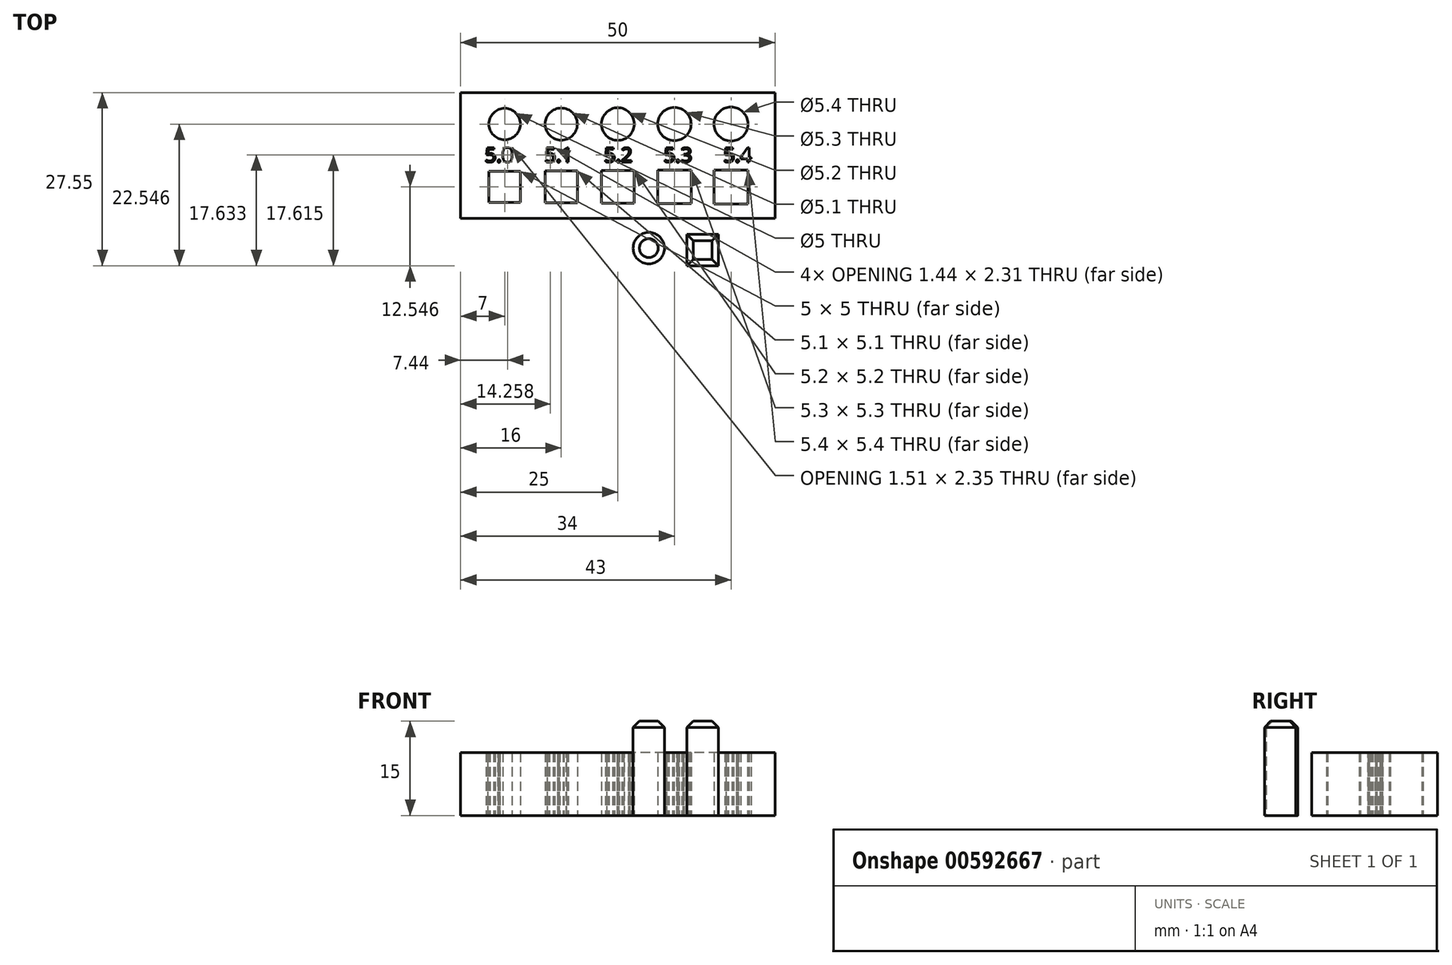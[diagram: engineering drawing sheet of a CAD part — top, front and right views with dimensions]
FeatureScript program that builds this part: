
annotation { "Feature Type Name" : "Feature", "Feature Type Description" : "" }
export const myFeature = defineFeature(function(context is Context, id is Id, definition is map)
    precondition{}
    {
        {
            var Q0;
            Q0=qCreatedBy(makeId("Top.planeOp"),FACE);
            var sketch = newSketch(context, id + "F0", { "sketchPlane" : qUnion([Q0])});
            skLineSegment(sketch, "E0.bottom", {"start": v(25, 24.5) * mm, "end": v(-25, 24.5) * mm});
            skLineSegment(sketch, "E0.top", {"start": v(25, 4.5) * mm, "end": v(-25, 4.5) * mm});
            skLineSegment(sketch, "E0.left", {"start": v(25, 24.5) * mm, "end": v(25, 4.5) * mm});
            skLineSegment(sketch, "E0.right", {"start": v(-25, 24.5) * mm, "end": v(-25, 4.5) * mm});
            skCircle(sketch, "E1", {"center": v(-18, 19.5) * mm, "radius": 2.5 * mm});
            skCircle(sketch, "E2", {"center": v(-9, 19.5) * mm, "radius": 2.55 * mm});
            skCircle(sketch, "E3", {"center": v(0, 19.5) * mm, "radius": 2.6 * mm});
            skLineSegment(sketch, "E4", {"start": v(-25, 19.5) * mm, "end": v(25, 19.5) * mm, "construction": true});
            skCircle(sketch, "E5", {"center": v(9, 19.5) * mm, "radius": 2.65 * mm});
            skCircle(sketch, "E6", {"center": v(18, 19.5) * mm, "radius": 2.7 * mm});
            skLineSegment(sketch, "E7", {"start": v(0, 24.5) * mm, "end": v(0, 4.5) * mm, "construction": true});
            skLineSegment(sketch, "E8.bottom", {"start": v(-15.5, 7) * mm, "end": v(-20.5, 7) * mm});
            skLineSegment(sketch, "E8.top", {"start": v(-15.5, 12) * mm, "end": v(-20.5, 12) * mm});
            skLineSegment(sketch, "E8.left", {"start": v(-15.5, 7) * mm, "end": v(-15.5, 12) * mm});
            skLineSegment(sketch, "E8.right", {"start": v(-20.5, 7) * mm, "end": v(-20.5, 12) * mm});
            skPoint(sketch, "E8.middle", {"position": v(-18, 9.5) * mm});
            skLineSegment(sketch, "E9.bottom", {"start": v(-6.45, 6.95) * mm, "end": v(-11.55, 6.95) * mm});
            skLineSegment(sketch, "E9.top", {"start": v(-6.45, 12.05) * mm, "end": v(-11.55, 12.05) * mm});
            skLineSegment(sketch, "E9.left", {"start": v(-6.45, 6.95) * mm, "end": v(-6.45, 12.05) * mm});
            skLineSegment(sketch, "E9.right", {"start": v(-11.55, 6.95) * mm, "end": v(-11.55, 12.05) * mm});
            skPoint(sketch, "E9.middle", {"position": v(-9, 9.5) * mm});
            skLineSegment(sketch, "E10.bottom", {"start": v(2.6, 6.9) * mm, "end": v(-2.6, 6.9) * mm});
            skLineSegment(sketch, "E10.top", {"start": v(2.6, 12.1) * mm, "end": v(-2.6, 12.1) * mm});
            skLineSegment(sketch, "E10.left", {"start": v(2.6, 6.9) * mm, "end": v(2.6, 12.1) * mm});
            skLineSegment(sketch, "E10.right", {"start": v(-2.6, 6.9) * mm, "end": v(-2.6, 12.1) * mm});
            skPoint(sketch, "E10.middle", {"position": v(0, 9.5) * mm});
            skLineSegment(sketch, "E11.bottom", {"start": v(11.65, 6.85) * mm, "end": v(6.35, 6.85) * mm});
            skLineSegment(sketch, "E11.top", {"start": v(11.65, 12.15) * mm, "end": v(6.35, 12.15) * mm});
            skLineSegment(sketch, "E11.left", {"start": v(11.65, 6.85) * mm, "end": v(11.65, 12.15) * mm});
            skLineSegment(sketch, "E11.right", {"start": v(6.35, 6.85) * mm, "end": v(6.35, 12.15) * mm});
            skPoint(sketch, "E11.middle", {"position": v(9, 9.5) * mm});
            skLineSegment(sketch, "E12.bottom", {"start": v(20.7, 6.8) * mm, "end": v(15.3, 6.8) * mm});
            skLineSegment(sketch, "E12.top", {"start": v(20.7, 12.2) * mm, "end": v(15.3, 12.2) * mm});
            skLineSegment(sketch, "E12.left", {"start": v(20.7, 6.8) * mm, "end": v(20.7, 12.2) * mm});
            skLineSegment(sketch, "E12.right", {"start": v(15.3, 6.8) * mm, "end": v(15.3, 12.2) * mm});
            skPoint(sketch, "E12.middle", {"position": v(18, 9.5) * mm});
            skLineSegment(sketch, "E13", {"start": v(-25, 9.5) * mm, "end": v(25, 9.5) * mm, "construction": true});
            skText(sketch, "E14", { "text": "5.0      5.1      5.2      5.3      5.4\n", "fontName": "OpenSans-Regular.ttf"});
            const initialGuessF0  = {"E14": [-0.02115, 0.01344, 1, 0, 0.0023]};
            skSetInitialGuess(sketch, initialGuessF0);
            skSolve(sketch);
        }
        {
            var Q0;
            Q0 = qSketchRegion(id + "F0", true);
            var Q1;
            Q1=makeQuery(id+"F0.imprint","IMPRINT",FACE,{"disambiguationData":[TD([[makeQuery(id+"F0.imprint","IMPRINT",EDGE,{"derivedFrom":sQuery(id+"F0.wireOp",EDGE,"E0.bottom")}),1.0]])]});
            extrude(context, id + "F1", {"entities" : qUnion([Q0, Q1]), "depth" : 10 * mm, "offsetDistance" : 25 * mm});
        }
        {
            var Q0;
            Q0=qCreatedBy(makeId("Top.planeOp"),FACE);
            var sketch = newSketch(context, id + "F2", { "sketchPlane" : qUnion([Q0])});
            skCircle(sketch, "E15", {"center": v(4.93, -0.25) * mm, "radius": 2.5 * mm});
            skLineSegment(sketch, "E16.bottom", {"start": v(15.98, -3.05) * mm, "end": v(10.98, -3.05) * mm});
            skLineSegment(sketch, "E16.top", {"start": v(15.98, 1.95) * mm, "end": v(10.98, 1.95) * mm});
            skLineSegment(sketch, "E16.left", {"start": v(15.98, -3.05) * mm, "end": v(15.98, 1.95) * mm});
            skLineSegment(sketch, "E16.right", {"start": v(10.98, -3.05) * mm, "end": v(10.98, 1.95) * mm});
            skPoint(sketch, "E16.middle", {"position": v(13.48, -0.55) * mm});
            skSolve(sketch);
        }
        {
            var Q0;
            Q0 = qSketchRegion(id + "F2", true);
            var Q1;
            Q1=makeQuery(id+"F2.imprint","IMPRINT",FACE,{"disambiguationData":[TD([[makeQuery(id+"F2.imprint","IMPRINT",EDGE,{"derivedFrom":sQuery(id+"F2.wireOp",EDGE,"E15")}),1.0]])]});
            extrude(context, id + "F3", {"entities" : qUnion([Q0, Q1]), "depth" : 15 * mm, "offsetDistance" : 25 * mm});
        }
        {
            var Q0;
            Q0=makeQuery(id+"F3.opExtrude","CAP_EDGE",EDGE,{"disambiguationData":[OSD([sQuery(id+"F2.wireOp",EDGE,"E15")])],"isStart":false});
            var Q1;
            Q1=makeQuery(id+"F3.opExtrude","CAP_EDGE",EDGE,{"disambiguationData":[OSD([sQuery(id+"F2.wireOp",EDGE,"E16.bottom")])],"isStart":false});
            var Q2;
            Q2=makeQuery(id+"F3.opExtrude","CAP_EDGE",EDGE,{"disambiguationData":[OSD([sQuery(id+"F2.wireOp",EDGE,"E16.right")])],"isStart":false});
            var Q3;
            Q3=makeQuery(id+"F3.opExtrude","CAP_EDGE",EDGE,{"disambiguationData":[OSD([sQuery(id+"F2.wireOp",EDGE,"E16.left")])],"isStart":false});
            var Q4;
            Q4=makeQuery(id+"F3.opExtrude","CAP_EDGE",EDGE,{"disambiguationData":[OSD([sQuery(id+"F2.wireOp",EDGE,"E16.top")])],"isStart":false});
            chamfer(context, id + "F4", {"entities" : qUnion([Q0, Q1, Q2, Q3, Q4]), "width" : 1 * mm, "tangentPropagation" : true});
        }
    });
